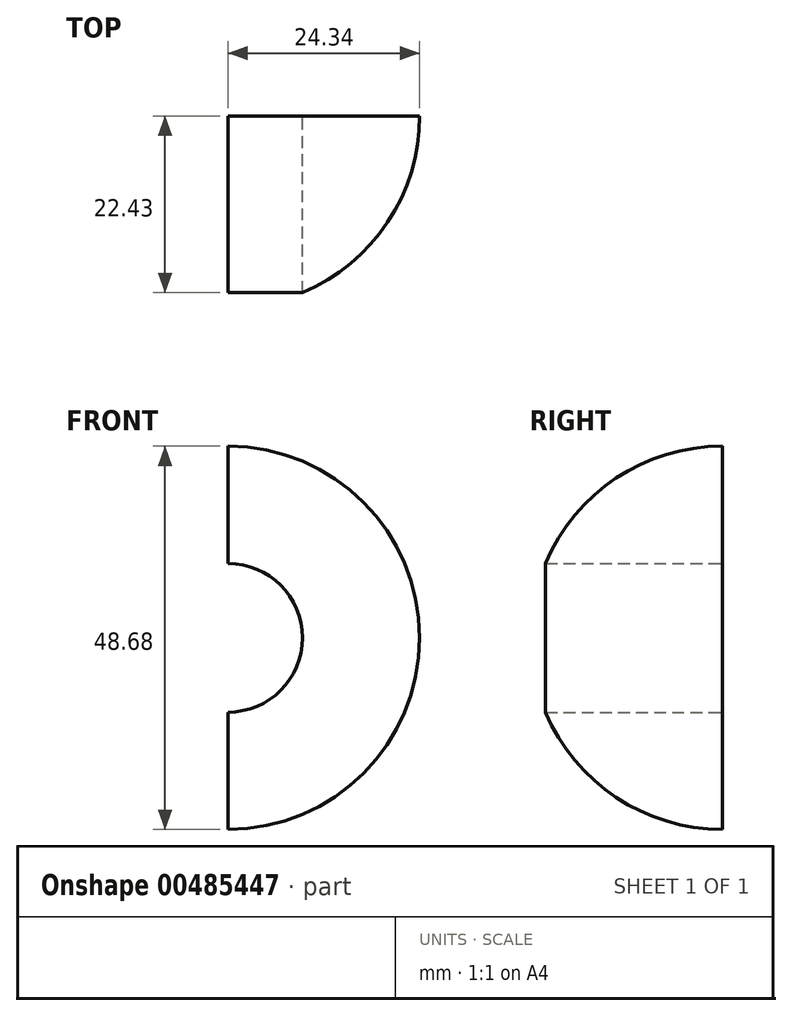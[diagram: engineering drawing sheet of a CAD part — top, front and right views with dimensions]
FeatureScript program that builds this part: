
annotation { "Feature Type Name" : "Feature", "Feature Type Description" : "" }
export const myFeature = defineFeature(function(context is Context, id is Id, definition is map)
    precondition{}
    {
        {
            var Q0;
            Q0=qCreatedBy(makeId("Front.planeOp"),FACE);
            var sketch = newSketch(context, id + "F0", { "sketchPlane" : qUnion([Q0])});
            skArc(sketch, "E0", {"start": v(0, 24.34) * mm, "mid": v(24.34, 0) * mm, "end": v(0, -24.34) * mm});
            skLineSegment(sketch, "E1", {"start": v(0, 24.34) * mm, "end": v(0, -24.34) * mm});
            skSolve(sketch);
        }
        {
            var Q0;
            Q0 = qSketchRegion(id + "F0", true);
            var Q1;
            Q1=sQuery(id+"F0.wireOp",EDGE,"E1");
            revolve(context, id + "F1", {"entities" : qUnion([Q0]), "axis" : qUnion([Q1]), "revolveType" : RevolveType.ONE_DIRECTION, "angle" : 90 * degree});
        }
        {
            var Q0;
            Q0=makeQuery(id+"F1.opRevolve","CAP_FACE",FACE,{"disambiguationData":[OSD([sQuery(id+"F0.wireOp",EDGE,"E0"),sQuery(id+"F0.wireOp",EDGE,"E1")])],"isStart":true});
            var sketch = newSketch(context, id + "F2", { "sketchPlane" : qUnion([Q0])});
            skCircle(sketch, "E2", {"center": v(0, 0) * mm, "radius": 9.45 * mm});
            skSolve(sketch);
        }
        {
            var Q0;
            Q0 = qSketchRegion(id + "F2", true);
            extrude(context, id + "F3", {"entities" : qUnion([Q0]), "operationType" : NewBodyOperationType.REMOVE, "endBound" : BoundingType.THROUGH_ALL, "oppositeDirection" : true, "depth" : 25.4 * mm});
        }
    });
